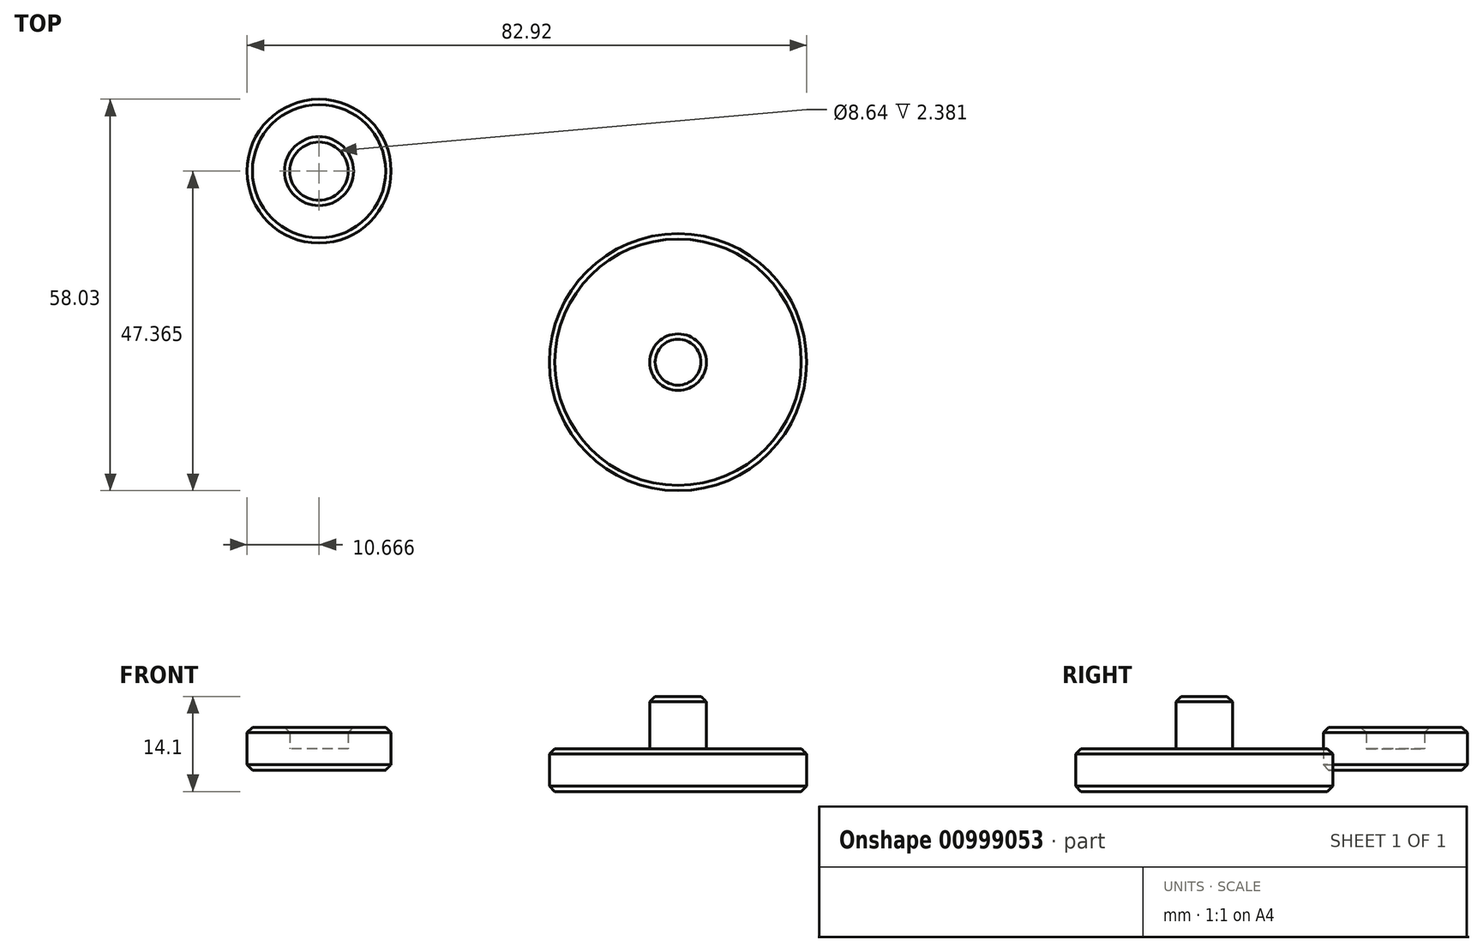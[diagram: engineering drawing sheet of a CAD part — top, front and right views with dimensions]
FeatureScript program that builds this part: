
annotation { "Feature Type Name" : "Feature", "Feature Type Description" : "" }
export const myFeature = defineFeature(function(context is Context, id is Id, definition is map)
    precondition{}
    {
        {
            var Q0;
            Q0=qCreatedBy(makeId("Top.planeOp"),FACE);
            var sketch = newSketch(context, id + "F0", { "sketchPlane" : qUnion([Q0])});
            skCircle(sketch, "E0", {"center": v(0, 0) * mm, "radius": 4.2 * mm});
            skCircle(sketch, "E1", {"center": v(0, 0) * mm, "radius": 19.05 * mm});
            skCircle(sketch, "E2", {"center": v(-53.2, 28.32) * mm, "radius": 10.67 * mm});
            skCircle(sketch, "E3", {"center": v(-53.2, 28.32) * mm, "radius": 4.32 * mm});
            skSolve(sketch);
        }
        {
            var Q0;
            Q0=makeQuery(id+"F0.imprint","IMPRINT",FACE,{"disambiguationData":[TD([[makeQuery(id+"F0.imprint","IMPRINT",EDGE,{"derivedFrom":sQuery(id+"F0.wireOp",EDGE,"E0")}),1.0]])]});
            extrude(context, id + "F1", {"entities" : qUnion([Q0]), "depth" : 7.75 * mm, "offsetDistance" : 25.4 * mm});
        }
        {
            var Q0;
            Q0=makeQuery(id+"F0.imprint","IMPRINT",FACE,{"disambiguationData":[TD([[makeQuery(id+"F0.imprint","IMPRINT",EDGE,{"derivedFrom":sQuery(id+"F0.wireOp",EDGE,"E0")}),1.0]])]});
            var Q1;
            Q1=makeQuery(id+"F0.imprint","IMPRINT",FACE,{"disambiguationData":[TD([[makeQuery(id+"F0.imprint","IMPRINT",EDGE,{"derivedFrom":sQuery(id+"F0.wireOp",EDGE,"E0")}),-1.0]])]});
            extrude(context, id + "F2", {"entities" : qUnion([Q0, Q1]), "operationType" : NewBodyOperationType.ADD, "oppositeDirection" : true, "depth" : 6.35 * mm, "offsetDistance" : 25.4 * mm});
        }
        {
            var Q0;
            Q0=makeQuery(id+"F0.imprint","IMPRINT",FACE,{"disambiguationData":[TD([[makeQuery(id+"F0.imprint","IMPRINT",EDGE,{"derivedFrom":sQuery(id+"F0.wireOp",EDGE,"E2")}),1.0]])]});
            extrude(context, id + "F3", {"entities" : qUnion([Q0]), "depth" : 3.17 * mm, "offsetDistance" : 25.4 * mm});
        }
        {
            var Q0;
            Q0=makeQuery(id+"F0.imprint","IMPRINT",FACE,{"disambiguationData":[TD([[makeQuery(id+"F0.imprint","IMPRINT",EDGE,{"derivedFrom":sQuery(id+"F0.wireOp",EDGE,"E3")}),1.0]])]});
            var Q1;
            Q1=makeQuery(id+"F0.imprint","IMPRINT",FACE,{"disambiguationData":[TD([[makeQuery(id+"F0.imprint","IMPRINT",EDGE,{"derivedFrom":sQuery(id+"F0.wireOp",EDGE,"E2")}),1.0]])]});
            extrude(context, id + "F4", {"entities" : qUnion([Q0, Q1]), "operationType" : NewBodyOperationType.ADD, "oppositeDirection" : true, "depth" : 3.17 * mm, "offsetDistance" : 25.4 * mm});
        }
        {
            var Q0;
            Q0=makeQuery(id+"F3.opExtrude","CAP_EDGE",EDGE,{"disambiguationData":[OSD([sQuery(id+"F0.wireOp",EDGE,"E2")])],"isStart":false});
            var Q1;
            Q1=makeQuery(id+"F3.opExtrude","CAP_EDGE",EDGE,{"disambiguationData":[OSD([sQuery(id+"F0.wireOp",EDGE,"E3")])],"isStart":true});
            var Q2;
            Q2=makeQuery(id+"F3.opExtrude","CAP_EDGE",EDGE,{"disambiguationData":[OSD([sQuery(id+"F0.wireOp",EDGE,"E3")])],"isStart":false});
            var Q3;
            Q3=makeQuery(id+"F4.opExtrude","CAP_EDGE",EDGE,{"disambiguationData":[OSD([sQuery(id+"F0.wireOp",EDGE,"E2")])],"isStart":false});
            var Q4;
            Q4=makeQuery(id+"F2.opExtrude","SWEPT_FACE",FACE,{"disambiguationData":[OSD([sQuery(id+"F0.wireOp",EDGE,"E1")])]});
            var Q5;
            Q5=makeQuery(id+"F1.opExtrude","CAP_FACE",FACE,{"disambiguationData":[OSD([sQuery(id+"F0.wireOp",EDGE,"E0")])],"isStart":false});
            chamfer(context, id + "F5", {"entities" : qUnion([Q0, Q1, Q2, Q3, Q4, Q5]), "width" : 0.8 * mm, "tangentPropagation" : true});
        }
    });
